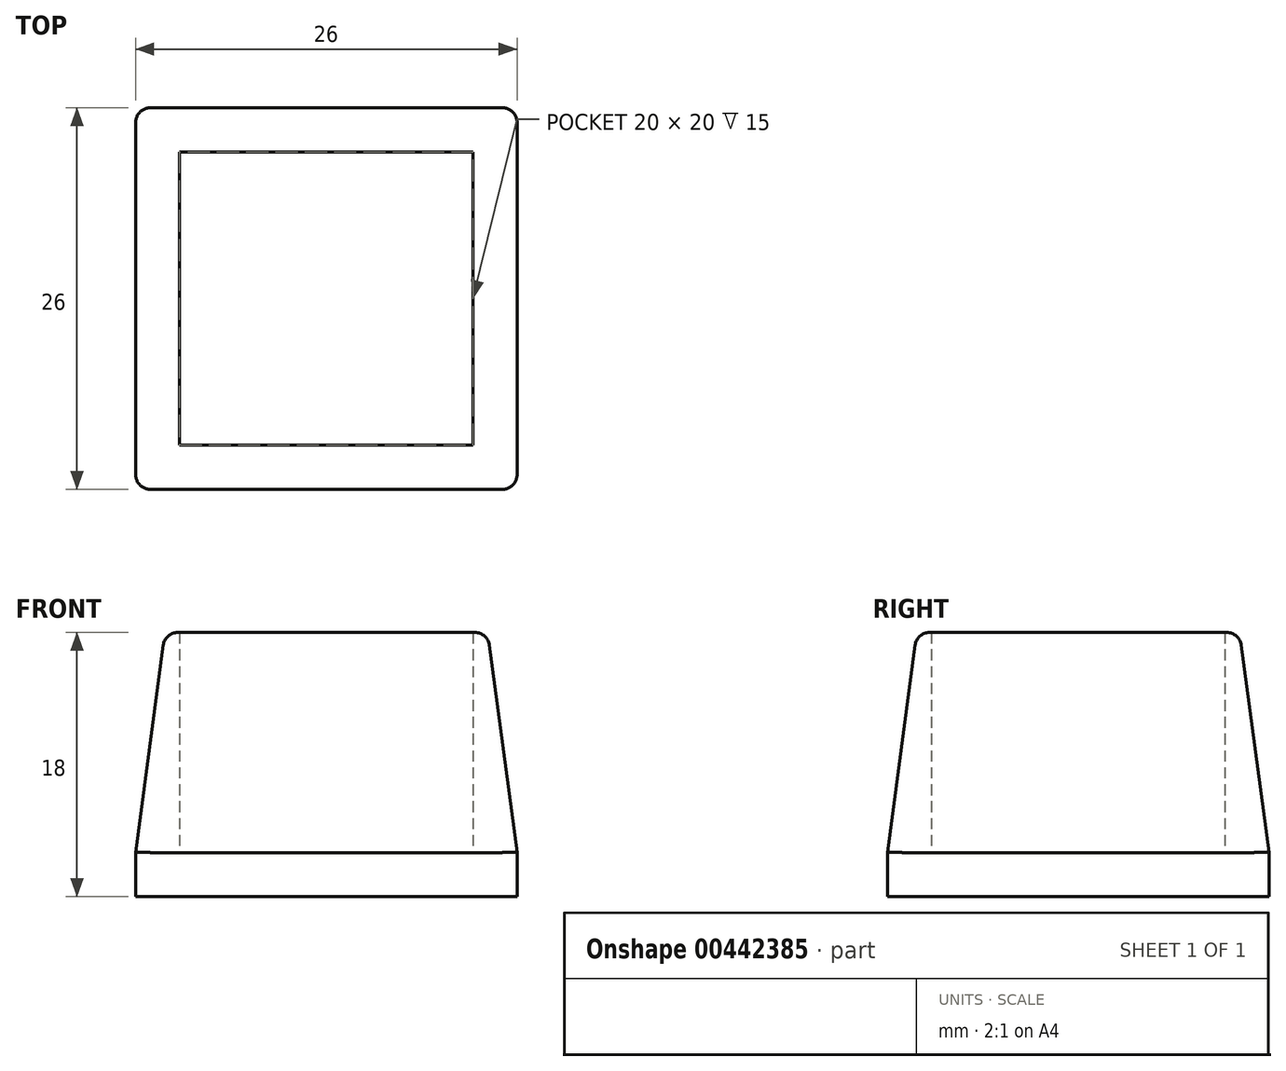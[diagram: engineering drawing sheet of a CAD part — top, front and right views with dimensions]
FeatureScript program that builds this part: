
annotation { "Feature Type Name" : "Feature", "Feature Type Description" : "" }
export const myFeature = defineFeature(function(context is Context, id is Id, definition is map)
    precondition{}
    {
        {
            var Q0;
            Q0=qCreatedBy(makeId("Top.planeOp"),FACE);
            var sketch = newSketch(context, id + "F0", { "sketchPlane" : qUnion([Q0])});
            skLineSegment(sketch, "E0.bottom", {"start": v(10, -10) * mm, "end": v(-10, -10) * mm});
            skLineSegment(sketch, "E0.top", {"start": v(10, 10) * mm, "end": v(-10, 10) * mm});
            skLineSegment(sketch, "E0.left", {"start": v(10, -10) * mm, "end": v(10, 10) * mm});
            skLineSegment(sketch, "E0.right", {"start": v(-10, -10) * mm, "end": v(-10, 10) * mm});
            skPoint(sketch, "E0.middle", {"position": v(0, 0) * mm});
            skLineSegment(sketch, "E1.0", {"start": v(13, -13) * mm, "end": v(13, 13) * mm});
            skLineSegment(sketch, "E1.1", {"start": v(13, -13) * mm, "end": v(-13, -13) * mm});
            skLineSegment(sketch, "E1.2", {"start": v(-13, -13) * mm, "end": v(-13, 13) * mm});
            skLineSegment(sketch, "E1.3", {"start": v(13, 13) * mm, "end": v(-13, 13) * mm});
            skSolve(sketch);
        }
        {
            var Q0;
            Q0=makeQuery(id+"F0.imprint","IMPRINT",FACE,{"disambiguationData":[TD([[makeQuery(id+"F0.imprint","IMPRINT",EDGE,{"derivedFrom":sQuery(id+"F0.wireOp",EDGE,"E0.bottom")}),-1.0]])]});
            extrude(context, id + "F1", {"entities" : qUnion([Q0]), "depth" : 3 * mm, "offsetDistance" : 25 * mm});
        }
        {
            var Q0;
            Q0=makeQuery(id+"F0.imprint","IMPRINT",FACE,{"disambiguationData":[TD([[makeQuery(id+"F0.imprint","IMPRINT",EDGE,{"derivedFrom":sQuery(id+"F0.wireOp",EDGE,"E0.bottom")}),1.0]])]});
            extrude(context, id + "F2", {"entities" : qUnion([Q0]), "operationType" : NewBodyOperationType.ADD, "depth" : 18 * mm, "offsetDistance" : 25 * mm});
        }
        {
            var Q0;
            Q0=makeQuery(id+"F2.opExtrude","CAP_EDGE",EDGE,{"disambiguationData":[OSD([sQuery(id+"F0.wireOp",EDGE,"E1.1")])],"isStart":false});
            var Q1;
            Q1=makeQuery(id+"F2.opExtrude","CAP_EDGE",EDGE,{"disambiguationData":[OSD([sQuery(id+"F0.wireOp",EDGE,"E1.0")])],"isStart":false});
            var Q2;
            Q2=makeQuery(id+"F2.opExtrude","CAP_EDGE",EDGE,{"disambiguationData":[OSD([sQuery(id+"F0.wireOp",EDGE,"E1.3")])],"isStart":false});
            var Q3;
            Q3=makeQuery(id+"F2.opExtrude","CAP_EDGE",EDGE,{"disambiguationData":[OSD([sQuery(id+"F0.wireOp",EDGE,"E1.2")])],"isStart":false});
            chamfer(context, id + "F3", {"entities" : qUnion([Q0, Q1, Q2, Q3]), "chamferType" : ChamferType.TWO_OFFSETS, "width1" : 15 * mm, "oppositeDirection" : false, "width2" : 2 * mm, "tangentPropagation" : true});
        }
        {
            var Q0;
            Q0=makeQuery(id+"F2.opExtrude","SWEPT_EDGE",EDGE,{"disambiguationData":[OSD([sQuery(id+"F0.wireOp",EDGE,"E1.0"),sQuery(id+"F0.wireOp",EDGE,"E1.1")])]});
            var Q1;
            Q1=makeQuery(id+"F3.opChamfer","BLEND_EDGE",EDGE,{"blendedFrom":[makeQuery(id+"F2.opExtrude","CAP_EDGE",EDGE,{"disambiguationData":[OSD([sQuery(id+"F0.wireOp",EDGE,"E1.0")])],"isStart":false}),makeQuery(id+"F2.opExtrude","CAP_EDGE",EDGE,{"disambiguationData":[OSD([sQuery(id+"F0.wireOp",EDGE,"E1.1")])],"isStart":false})],"blendedInto":[]});
            var Q2;
            Q2=makeQuery(id+"F2.opExtrude","SWEPT_EDGE",EDGE,{"disambiguationData":[OSD([sQuery(id+"F0.wireOp",EDGE,"E1.0"),sQuery(id+"F0.wireOp",EDGE,"E1.3")])]});
            var Q3;
            Q3=makeQuery(id+"F3.opChamfer","BLEND_EDGE",EDGE,{"blendedFrom":[makeQuery(id+"F2.opExtrude","CAP_EDGE",EDGE,{"disambiguationData":[OSD([sQuery(id+"F0.wireOp",EDGE,"E1.0")])],"isStart":false}),makeQuery(id+"F2.opExtrude","CAP_EDGE",EDGE,{"disambiguationData":[OSD([sQuery(id+"F0.wireOp",EDGE,"E1.3")])],"isStart":false})],"blendedInto":[]});
            var Q4;
            Q4=makeQuery(id+"F2.opExtrude","SWEPT_EDGE",EDGE,{"disambiguationData":[OSD([sQuery(id+"F0.wireOp",EDGE,"E1.2"),sQuery(id+"F0.wireOp",EDGE,"E1.3")])]});
            var Q5;
            Q5=makeQuery(id+"F3.opChamfer","BLEND_EDGE",EDGE,{"blendedFrom":[makeQuery(id+"F2.opExtrude","CAP_EDGE",EDGE,{"disambiguationData":[OSD([sQuery(id+"F0.wireOp",EDGE,"E1.2")])],"isStart":false}),makeQuery(id+"F2.opExtrude","CAP_EDGE",EDGE,{"disambiguationData":[OSD([sQuery(id+"F0.wireOp",EDGE,"E1.3")])],"isStart":false})],"blendedInto":[]});
            var Q6;
            Q6=makeQuery(id+"F3.opChamfer","BLEND_EDGE",EDGE,{"blendedFrom":[makeQuery(id+"F2.opExtrude","CAP_EDGE",EDGE,{"disambiguationData":[OSD([sQuery(id+"F0.wireOp",EDGE,"E1.1")])],"isStart":false}),makeQuery(id+"F2.opExtrude","CAP_EDGE",EDGE,{"disambiguationData":[OSD([sQuery(id+"F0.wireOp",EDGE,"E1.2")])],"isStart":false})],"blendedInto":[]});
            var Q7;
            Q7=makeQuery(id+"F2.opExtrude","SWEPT_EDGE",EDGE,{"disambiguationData":[OSD([sQuery(id+"F0.wireOp",EDGE,"E1.1"),sQuery(id+"F0.wireOp",EDGE,"E1.2")])]});
            var Q8;
            {var subQ0=sQuery(id+"F0.wireOp",EDGE,"E1.1");Q8=makeQuery(id+"F3.opChamfer","BLEND_EDGE",EDGE,{"blendedFrom":[makeQuery(id+"F2.opExtrude","CAP_EDGE",EDGE,{"disambiguationData":[OSD([subQ0])],"isStart":false}),makeQuery(id+"F2.opExtrude","CAP_FACE",FACE,{"disambiguationData":[OSD([sQuery(id+"F0.wireOp",EDGE,"E0.bottom"),sQuery(id+"F0.wireOp",EDGE,"E0.top"),sQuery(id+"F0.wireOp",EDGE,"E0.left"),sQuery(id+"F0.wireOp",EDGE,"E0.right"),sQuery(id+"F0.wireOp",EDGE,"E1.0"),subQ0,sQuery(id+"F0.wireOp",EDGE,"E1.2"),sQuery(id+"F0.wireOp",EDGE,"E1.3")])],"isStart":false})],"blendedInto":[makeQuery(id+"F2.opExtrude","CAP_FACE",FACE,{"disambiguationData":[OSD([sQuery(id+"F0.wireOp",EDGE,"E0.bottom"),sQuery(id+"F0.wireOp",EDGE,"E0.top"),sQuery(id+"F0.wireOp",EDGE,"E0.left"),sQuery(id+"F0.wireOp",EDGE,"E0.right"),sQuery(id+"F0.wireOp",EDGE,"E1.0"),subQ0,sQuery(id+"F0.wireOp",EDGE,"E1.2"),sQuery(id+"F0.wireOp",EDGE,"E1.3")])],"isStart":false})]});}
            var Q9;
            {var subQ0=sQuery(id+"F0.wireOp",EDGE,"E1.0");Q9=makeQuery(id+"F3.opChamfer","BLEND_EDGE",EDGE,{"blendedFrom":[makeQuery(id+"F2.opExtrude","CAP_EDGE",EDGE,{"disambiguationData":[OSD([subQ0])],"isStart":false}),makeQuery(id+"F2.opExtrude","CAP_FACE",FACE,{"disambiguationData":[OSD([sQuery(id+"F0.wireOp",EDGE,"E0.bottom"),sQuery(id+"F0.wireOp",EDGE,"E0.top"),sQuery(id+"F0.wireOp",EDGE,"E0.left"),sQuery(id+"F0.wireOp",EDGE,"E0.right"),subQ0,sQuery(id+"F0.wireOp",EDGE,"E1.1"),sQuery(id+"F0.wireOp",EDGE,"E1.2"),sQuery(id+"F0.wireOp",EDGE,"E1.3")])],"isStart":false})],"blendedInto":[makeQuery(id+"F2.opExtrude","CAP_FACE",FACE,{"disambiguationData":[OSD([sQuery(id+"F0.wireOp",EDGE,"E0.bottom"),sQuery(id+"F0.wireOp",EDGE,"E0.top"),sQuery(id+"F0.wireOp",EDGE,"E0.left"),sQuery(id+"F0.wireOp",EDGE,"E0.right"),subQ0,sQuery(id+"F0.wireOp",EDGE,"E1.1"),sQuery(id+"F0.wireOp",EDGE,"E1.2"),sQuery(id+"F0.wireOp",EDGE,"E1.3")])],"isStart":false})]});}
            var Q10;
            {var subQ0=sQuery(id+"F0.wireOp",EDGE,"E1.3");Q10=makeQuery(id+"F3.opChamfer","BLEND_EDGE",EDGE,{"blendedFrom":[makeQuery(id+"F2.opExtrude","CAP_EDGE",EDGE,{"disambiguationData":[OSD([subQ0])],"isStart":false}),makeQuery(id+"F2.opExtrude","CAP_FACE",FACE,{"disambiguationData":[OSD([sQuery(id+"F0.wireOp",EDGE,"E0.bottom"),sQuery(id+"F0.wireOp",EDGE,"E0.top"),sQuery(id+"F0.wireOp",EDGE,"E0.left"),sQuery(id+"F0.wireOp",EDGE,"E0.right"),sQuery(id+"F0.wireOp",EDGE,"E1.0"),sQuery(id+"F0.wireOp",EDGE,"E1.1"),sQuery(id+"F0.wireOp",EDGE,"E1.2"),subQ0])],"isStart":false})],"blendedInto":[makeQuery(id+"F2.opExtrude","CAP_FACE",FACE,{"disambiguationData":[OSD([sQuery(id+"F0.wireOp",EDGE,"E0.bottom"),sQuery(id+"F0.wireOp",EDGE,"E0.top"),sQuery(id+"F0.wireOp",EDGE,"E0.left"),sQuery(id+"F0.wireOp",EDGE,"E0.right"),sQuery(id+"F0.wireOp",EDGE,"E1.0"),sQuery(id+"F0.wireOp",EDGE,"E1.1"),sQuery(id+"F0.wireOp",EDGE,"E1.2"),subQ0])],"isStart":false})]});}
            var Q11;
            {var subQ0=sQuery(id+"F0.wireOp",EDGE,"E1.2");Q11=makeQuery(id+"F3.opChamfer","BLEND_EDGE",EDGE,{"blendedFrom":[makeQuery(id+"F2.opExtrude","CAP_EDGE",EDGE,{"disambiguationData":[OSD([subQ0])],"isStart":false}),makeQuery(id+"F2.opExtrude","CAP_FACE",FACE,{"disambiguationData":[OSD([sQuery(id+"F0.wireOp",EDGE,"E0.bottom"),sQuery(id+"F0.wireOp",EDGE,"E0.top"),sQuery(id+"F0.wireOp",EDGE,"E0.left"),sQuery(id+"F0.wireOp",EDGE,"E0.right"),sQuery(id+"F0.wireOp",EDGE,"E1.0"),sQuery(id+"F0.wireOp",EDGE,"E1.1"),subQ0,sQuery(id+"F0.wireOp",EDGE,"E1.3")])],"isStart":false})],"blendedInto":[makeQuery(id+"F2.opExtrude","CAP_FACE",FACE,{"disambiguationData":[OSD([sQuery(id+"F0.wireOp",EDGE,"E0.bottom"),sQuery(id+"F0.wireOp",EDGE,"E0.top"),sQuery(id+"F0.wireOp",EDGE,"E0.left"),sQuery(id+"F0.wireOp",EDGE,"E0.right"),sQuery(id+"F0.wireOp",EDGE,"E1.0"),sQuery(id+"F0.wireOp",EDGE,"E1.1"),subQ0,sQuery(id+"F0.wireOp",EDGE,"E1.3")])],"isStart":false})]});}
            fillet(context, id + "F4", {"entities" : qUnion([Q0, Q1, Q2, Q3, Q4, Q5, Q6, Q7, Q8, Q9, Q10, Q11]), "tangentPropagation" : true, "radius" : 1 * mm, "defaultsChanged" : true, "vertexSettings" : [], "allowEdgeOverflow" : false});
        }
    });
